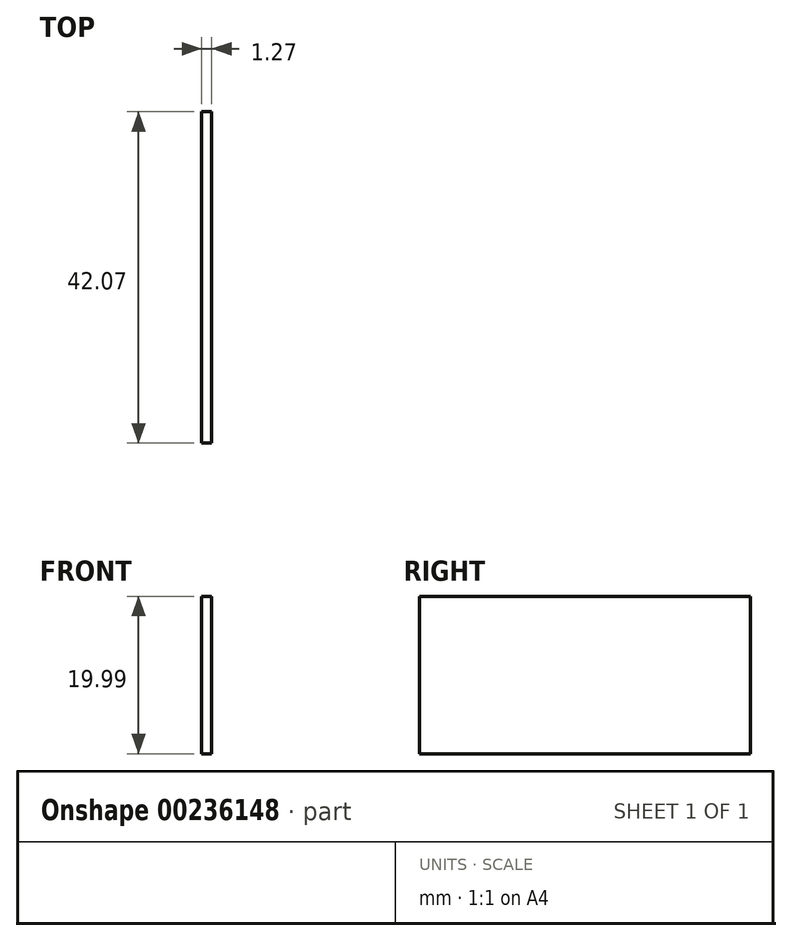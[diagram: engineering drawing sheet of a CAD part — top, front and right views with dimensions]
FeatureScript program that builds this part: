
annotation { "Feature Type Name" : "Feature", "Feature Type Description" : "" }
export const myFeature = defineFeature(function(context is Context, id is Id, definition is map)
    precondition{}
    {
        {
            var Q0;
            Q0=qCreatedBy(makeId("Right.planeOp"),FACE);
            var sketch = newSketch(context, id + "F0", { "sketchPlane" : qUnion([Q0])});
            skLineSegment(sketch, "E0.bottom", {"start": v(-36.56, 13.33) * mm, "end": v(5.5, 13.33) * mm});
            skLineSegment(sketch, "E0.top", {"start": v(-36.56, -6.66) * mm, "end": v(5.5, -6.66) * mm});
            skLineSegment(sketch, "E0.left", {"start": v(-36.56, 13.33) * mm, "end": v(-36.56, -6.66) * mm});
            skLineSegment(sketch, "E0.right", {"start": v(5.5, 13.33) * mm, "end": v(5.5, -6.66) * mm});
            skSolve(sketch);
        }
        {
            var Q0;
            Q0 = qSketchRegion(id + "F0", true);
            extrude(context, id + "F1", {"entities" : qUnion([Q0]), "depth" : 1.27 * mm});
        }
    });
